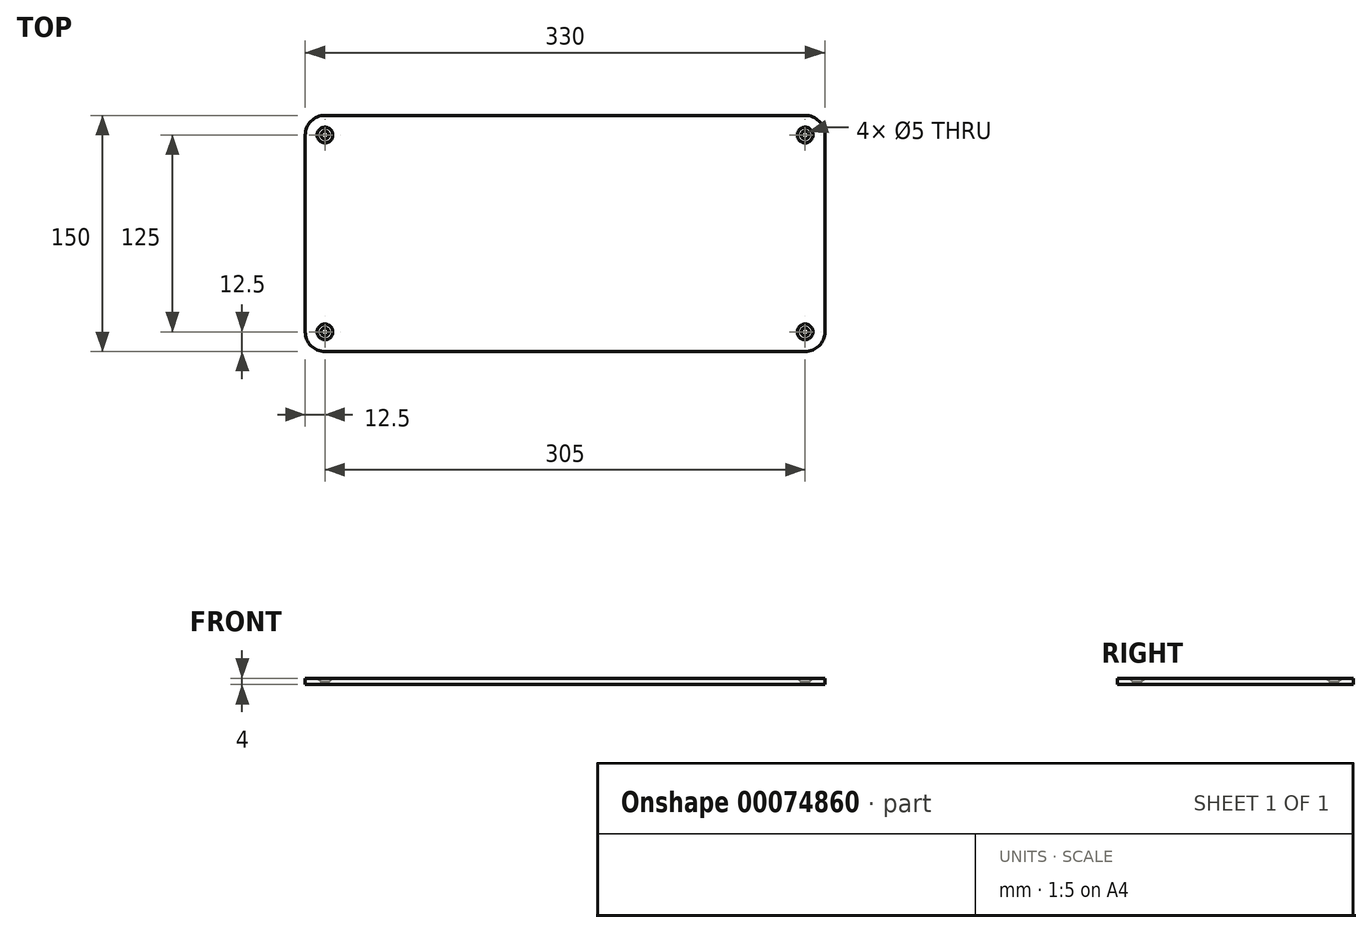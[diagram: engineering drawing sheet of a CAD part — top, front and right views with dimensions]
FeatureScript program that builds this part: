
annotation { "Feature Type Name" : "Feature", "Feature Type Description" : "" }
export const myFeature = defineFeature(function(context is Context, id is Id, definition is map)
    precondition{}
    {
        {
            var Q0;
            Q0=qCreatedBy(makeId("Top.planeOp"),FACE);
            var sketch = newSketch(context, id + "F0", { "sketchPlane" : qUnion([Q0])});
            skLineSegment(sketch, "E0.bottom", {"start": v(0, 0) * mm, "end": v(330, 0) * mm});
            skLineSegment(sketch, "E0.top", {"start": v(0, 150) * mm, "end": v(330, 150) * mm});
            skLineSegment(sketch, "E0.left", {"start": v(0, 0) * mm, "end": v(0, 150) * mm});
            skLineSegment(sketch, "E0.right", {"start": v(330, 0) * mm, "end": v(330, 150) * mm});
            skSolve(sketch);
        }
        {
            var Q0;
            Q0=makeQuery(id+"F0.imprint","IMPRINT",FACE,{"disambiguationData":[TD([[makeQuery(id+"F0.imprint","IMPRINT",EDGE,{"derivedFrom":sQuery(id+"F0.wireOp",EDGE,"E0.bottom")}),1.0]])]});
            extrude(context, id + "F1", {"entities" : qUnion([Q0]), "depth" : 4 * mm});
        }
        {
            var Q0;
            Q0=makeQuery(id+"F1.opExtrude","SWEPT_EDGE",EDGE,{"disambiguationData":[OSD([sQuery(id+"F0.wireOp",EDGE,"E0.bottom"),sQuery(id+"F0.wireOp",EDGE,"E0.right")])]});
            var Q1;
            Q1=makeQuery(id+"F1.opExtrude","SWEPT_EDGE",EDGE,{"disambiguationData":[OSD([sQuery(id+"F0.wireOp",EDGE,"E0.top"),sQuery(id+"F0.wireOp",EDGE,"E0.right")])]});
            var Q2;
            Q2=makeQuery(id+"F1.opExtrude","SWEPT_EDGE",EDGE,{"disambiguationData":[OSD([sQuery(id+"F0.wireOp",EDGE,"E0.top"),sQuery(id+"F0.wireOp",EDGE,"E0.left")])]});
            var Q3;
            Q3=makeQuery(id+"F1.opExtrude","SWEPT_EDGE",EDGE,{"disambiguationData":[OSD([sQuery(id+"F0.wireOp",EDGE,"E0.bottom"),sQuery(id+"F0.wireOp",EDGE,"E0.left")])]});
            fillet(context, id + "F2", {"entities" : qUnion([Q0, Q1, Q2, Q3]), "radius" : 12.5 * mm, "tangentPropagation" : true, "allowEdgeOverflow" : false});
        }
        {
            var Q0;
            Q0=makeQuery(id+"F1.opExtrude","CAP_FACE",FACE,{"disambiguationData":[OSD([sQuery(id+"F0.wireOp",EDGE,"E0.bottom"),sQuery(id+"F0.wireOp",EDGE,"E0.top"),sQuery(id+"F0.wireOp",EDGE,"E0.left"),sQuery(id+"F0.wireOp",EDGE,"E0.right")])],"isStart":false});
            var sketch = newSketch(context, id + "F3", { "sketchPlane" : qUnion([Q0])});
            skCircle(sketch, "E1", {"center": v(12.5, 12.5) * mm, "radius": 2.5 * mm});
            skCircle(sketch, "E2", {"center": v(12.5, 137.5) * mm, "radius": 2.5 * mm});
            skCircle(sketch, "E3", {"center": v(317.5, 137.5) * mm, "radius": 2.5 * mm});
            skCircle(sketch, "E4", {"center": v(317.5, 12.5) * mm, "radius": 2.5 * mm});
            skSolve(sketch);
        }
        {
            var Q0;
            Q0=sQuery(id+"F3.wireOp",VERTEX,"E2.center");
            var Q1;
            Q1=sQuery(id+"F3.wireOp",VERTEX,"E3.center");
            var Q2;
            Q2=sQuery(id+"F3.wireOp",VERTEX,"E4.center");
            var Q3;
            Q3=sQuery(id+"F3.wireOp",VERTEX,"E1.center");
            var Q4;
            Q4=makeQuery(id+"F1.opExtrude","SWEPT_BODY",BODY,{"disambiguationData":[OSD([sQuery(id+"F0.wireOp",EDGE,"E0.bottom"),sQuery(id+"F0.wireOp",EDGE,"E0.top"),sQuery(id+"F0.wireOp",EDGE,"E0.left"),sQuery(id+"F0.wireOp",EDGE,"E0.right")])]});
            hole(context, id + "F4", {"style" : HoleStyle.C_SINK, "endStyle" : HoleEndStyle.THROUGH, "holeDiameter" : 5 * mm, "cSinkDiameter" : 10 * mm, "cSinkAngle" : 90 * degree, "locations" : qUnion([Q0, Q1, Q2, Q3]), "scope" : qUnion([Q4]), "isTappedThrough" : true});
        }
    });
